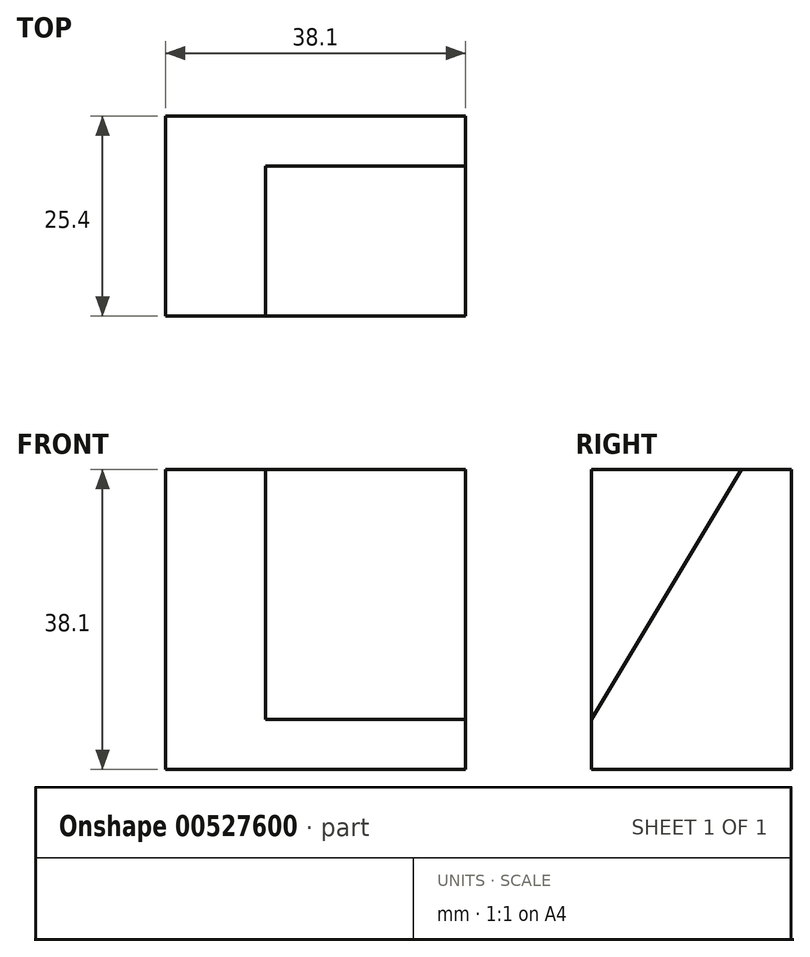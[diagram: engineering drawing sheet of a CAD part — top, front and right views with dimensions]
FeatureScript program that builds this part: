
annotation { "Feature Type Name" : "Feature", "Feature Type Description" : "" }
export const myFeature = defineFeature(function(context is Context, id is Id, definition is map)
    precondition{}
    {
        {
            var Q0;
            Q0=qCreatedBy(makeId("Right.planeOp"),FACE);
            var sketch = newSketch(context, id + "F0", { "sketchPlane" : qUnion([Q0])});
            skLineSegment(sketch, "E0", {"start": v(0, 0) * mm, "end": v(25.4, 0) * mm});
            skLineSegment(sketch, "E1", {"start": v(25.4, 0) * mm, "end": v(25.4, 38.1) * mm});
            skLineSegment(sketch, "E2", {"start": v(25.4, 38.1) * mm, "end": v(0, 38.1) * mm});
            skLineSegment(sketch, "E3", {"start": v(0, 38.1) * mm, "end": v(0, 0) * mm});
            skSolve(sketch);
        }
        {
            var Q0;
            Q0 = qSketchRegion(id + "F0", true);
            extrude(context, id + "F1", {"entities" : qUnion([Q0]), "depth" : 38.1 * mm, "offsetDistance" : 25.4 * mm});
        }
        {
            var Q0;
            Q0=makeQuery(id+"F1.opExtrude","CAP_FACE",FACE,{"disambiguationData":[OSD([sQuery(id+"F0.wireOp",EDGE,"E0"),sQuery(id+"F0.wireOp",EDGE,"E1"),sQuery(id+"F0.wireOp",EDGE,"E2"),sQuery(id+"F0.wireOp",EDGE,"E3")])],"isStart":false});
            var sketch = newSketch(context, id + "F2", { "sketchPlane" : qUnion([Q0])});
            skLineSegment(sketch, "E4", {"start": v(0, 6.35) * mm, "end": v(19.05, 38.1) * mm});
            skSolve(sketch);
        }
        {
            var Q0;
            Q0 = qSketchRegion(id + "F2", true);
            var Q1;
            {var subQ0=sQuery(id+"F2.wireOp",EDGE,"E4");Q1=makeQuery(id+"F2.imprint","IMPRINT",FACE,{"disambiguationData":[TD([[makeQuery(id+"F2.imprint","IMPRINT",EDGE,{"derivedFrom":subQ0}),1.0]])]});}
            extrude(context, id + "F3", {"entities" : qUnion([Q0, Q1]), "operationType" : NewBodyOperationType.REMOVE, "oppositeDirection" : true, "depth" : 25.4 * mm, "offsetDistance" : 25.4 * mm});
        }
    });
